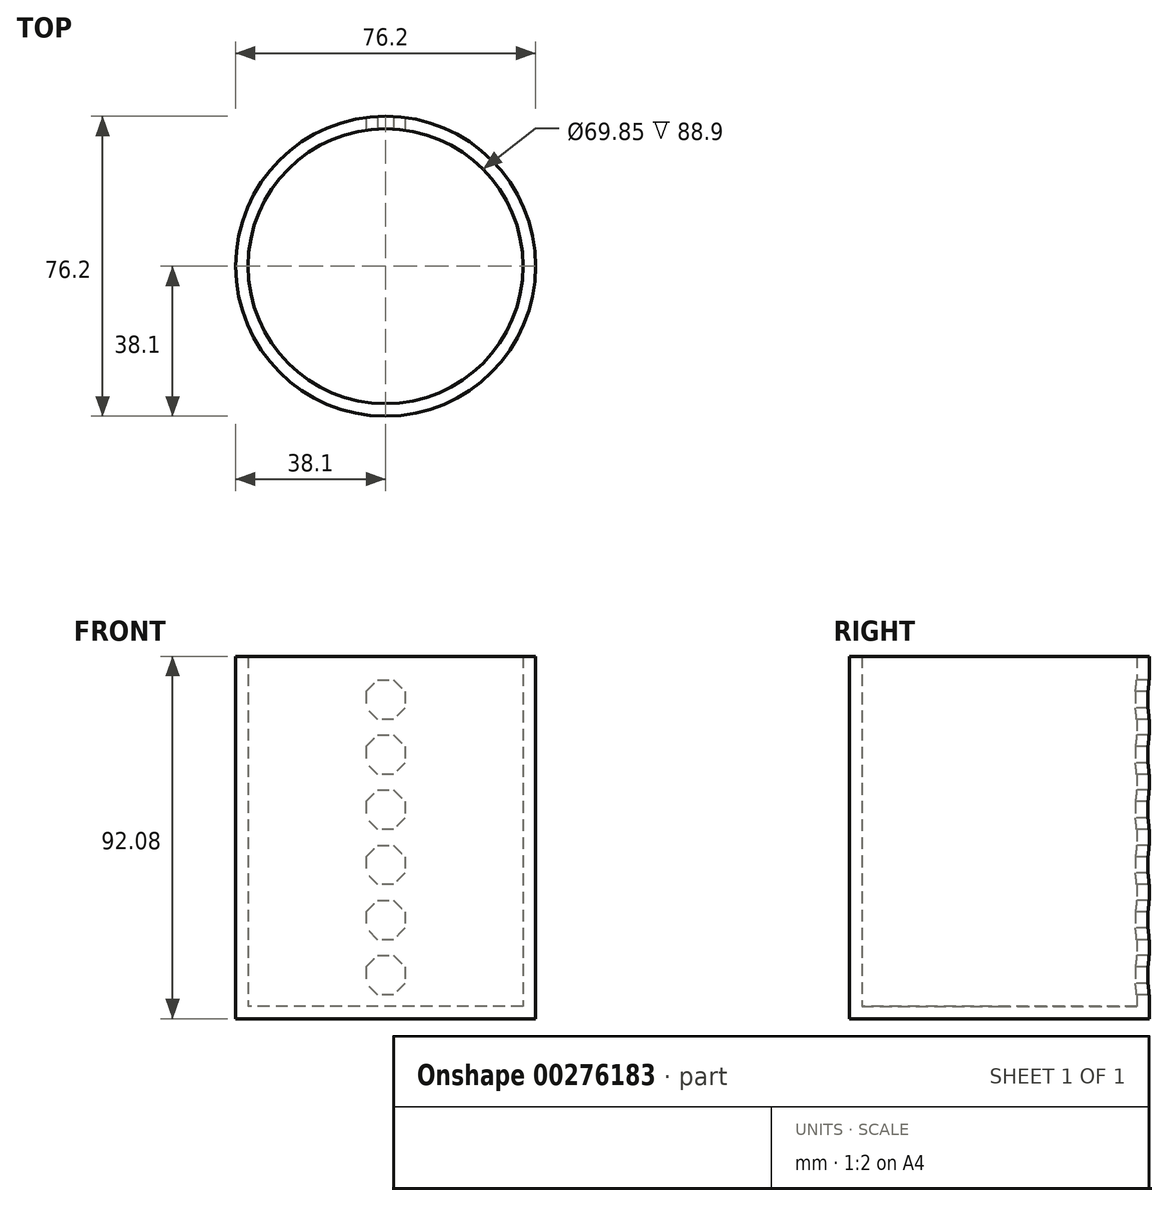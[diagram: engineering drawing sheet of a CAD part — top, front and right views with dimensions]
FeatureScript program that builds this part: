
annotation { "Feature Type Name" : "Feature", "Feature Type Description" : "" }
export const myFeature = defineFeature(function(context is Context, id is Id, definition is map)
    precondition{}
    {
        {
            var Q0;
            Q0=qCreatedBy(makeId("Top.planeOp"),FACE);
            var sketch = newSketch(context, id + "F0", { "sketchPlane" : qUnion([Q0])});
            skCircle(sketch, "E0", {"center": v(0, 0) * mm, "radius": 38.1 * mm});
            skSolve(sketch);
        }
        {
            var Q0;
            Q0=qSketchRegion(id+"F0",true);
            extrude(context, id + "F1", {"entities" : qUnion([Q0]), "depth" : 3.17 * mm});
        }
        {
            var Q0;
            Q0=makeQuery(id+"F1.opExtrude","CAP_FACE",FACE,{"disambiguationData":[OSD([sQuery(id+"F0.wireOp",EDGE,"E0")])],"isStart":false});
            var sketch = newSketch(context, id + "F2", { "sketchPlane" : qUnion([Q0])});
            skCircle(sketch, "E1.0", {"center": v(0, 0) * mm, "radius": 38.1 * mm});
            skCircle(sketch, "E2.0", {"center": v(0, 0) * mm, "radius": 34.93 * mm});
            skSolve(sketch);
        }
        {
            var Q0;
            Q0=qSketchRegion(id+"F2",true);
            extrude(context, id + "F3", {"entities" : qUnion([Q0]), "operationType" : NewBodyOperationType.ADD, "depth" : 88.9 * mm});
        }
        {
            var Q0;
            Q0=qCreatedBy(makeId("Right.planeOp"),FACE);
            var sketch = newSketch(context, id + "F4", { "sketchPlane" : qUnion([Q0])});
            skLineSegment(sketch, "E3", {"start": v(0, 0) * mm, "end": v(0, 120.33) * mm});
            skSolve(sketch);
        }
        {
            var Q0;
            Q0=qCreatedBy(makeId("Front.planeOp"),FACE);
            var sketch = newSketch(context, id + "F5", { "sketchPlane" : qUnion([Q0])});
            skCircle(sketch, "E4.cCircle", {"center": v(0, 81.08) * mm, "radius": 5 * mm, "construction": true});
            skLineSegment(sketch, "E4.0", {"start": v(2.07, 86.07) * mm, "end": v(5, 83.15) * mm});
            skLineSegment(sketch, "E4.1", {"start": v(5, 83.15) * mm, "end": v(5, 79) * mm});
            skLineSegment(sketch, "E4.2", {"start": v(5, 79) * mm, "end": v(2.07, 76.08) * mm});
            skLineSegment(sketch, "E4.3", {"start": v(2.07, 76.08) * mm, "end": v(-2.07, 76.08) * mm});
            skLineSegment(sketch, "E4.4", {"start": v(-2.07, 76.08) * mm, "end": v(-5, 79) * mm});
            skLineSegment(sketch, "E4.5", {"start": v(-5, 79) * mm, "end": v(-5, 83.15) * mm});
            skLineSegment(sketch, "E4.6", {"start": v(-5, 83.15) * mm, "end": v(-2.07, 86.08) * mm});
            skLineSegment(sketch, "E4.7", {"start": v(-2.07, 86.08) * mm, "end": v(2.07, 86.08) * mm});
            skPoint(sketch, "E4.0.midPoint", {"position": v(3.54, 84.61) * mm});
            skLineSegment(sketch, "E5.0.1.0", {"start": v(-2.07, 72.08) * mm, "end": v(2.07, 72.08) * mm});
            skLineSegment(sketch, "E5.0.1.1", {"start": v(2.07, 72.07) * mm, "end": v(5, 69.15) * mm});
            skLineSegment(sketch, "E5.0.1.2", {"start": v(5, 69.15) * mm, "end": v(5, 65) * mm});
            skLineSegment(sketch, "E5.0.1.3", {"start": v(5, 65) * mm, "end": v(2.07, 62.08) * mm});
            skLineSegment(sketch, "E5.0.1.4", {"start": v(2.07, 62.08) * mm, "end": v(-2.07, 62.08) * mm});
            skLineSegment(sketch, "E5.0.1.5", {"start": v(-2.07, 62.08) * mm, "end": v(-5, 65) * mm});
            skLineSegment(sketch, "E5.0.1.6", {"start": v(-5, 65) * mm, "end": v(-5, 69.15) * mm});
            skLineSegment(sketch, "E5.0.1.7", {"start": v(-5, 69.15) * mm, "end": v(-2.07, 72.08) * mm});
            skLineSegment(sketch, "E5.0.2.0", {"start": v(-2.07, 58.08) * mm, "end": v(2.07, 58.08) * mm});
            skLineSegment(sketch, "E5.0.2.1", {"start": v(2.07, 58.07) * mm, "end": v(5, 55.15) * mm});
            skLineSegment(sketch, "E5.0.2.2", {"start": v(5, 55.15) * mm, "end": v(5, 51) * mm});
            skLineSegment(sketch, "E5.0.2.3", {"start": v(5, 51) * mm, "end": v(2.07, 48.08) * mm});
            skLineSegment(sketch, "E5.0.2.4", {"start": v(2.07, 48.08) * mm, "end": v(-2.07, 48.08) * mm});
            skLineSegment(sketch, "E5.0.2.5", {"start": v(-2.07, 48.08) * mm, "end": v(-5, 51) * mm});
            skLineSegment(sketch, "E5.0.2.6", {"start": v(-5, 51) * mm, "end": v(-5, 55.15) * mm});
            skLineSegment(sketch, "E5.0.2.7", {"start": v(-5, 55.15) * mm, "end": v(-2.07, 58.08) * mm});
            skLineSegment(sketch, "E5.0.3.0", {"start": v(-2.07, 44.08) * mm, "end": v(2.07, 44.08) * mm});
            skLineSegment(sketch, "E5.0.3.1", {"start": v(2.07, 44.07) * mm, "end": v(5, 41.15) * mm});
            skLineSegment(sketch, "E5.0.3.2", {"start": v(5, 41.15) * mm, "end": v(5, 37) * mm});
            skLineSegment(sketch, "E5.0.3.3", {"start": v(5, 37) * mm, "end": v(2.07, 34.08) * mm});
            skLineSegment(sketch, "E5.0.3.4", {"start": v(2.07, 34.08) * mm, "end": v(-2.07, 34.08) * mm});
            skLineSegment(sketch, "E5.0.3.5", {"start": v(-2.07, 34.08) * mm, "end": v(-5, 37) * mm});
            skLineSegment(sketch, "E5.0.3.6", {"start": v(-5, 37) * mm, "end": v(-5, 41.15) * mm});
            skLineSegment(sketch, "E5.0.3.7", {"start": v(-5, 41.15) * mm, "end": v(-2.07, 44.08) * mm});
            skLineSegment(sketch, "E5.0.4.0", {"start": v(-2.07, 30.08) * mm, "end": v(2.07, 30.08) * mm});
            skLineSegment(sketch, "E5.0.4.1", {"start": v(2.07, 30.07) * mm, "end": v(5, 27.15) * mm});
            skLineSegment(sketch, "E5.0.4.2", {"start": v(5, 27.15) * mm, "end": v(5, 23) * mm});
            skLineSegment(sketch, "E5.0.4.3", {"start": v(5, 23) * mm, "end": v(2.07, 20.08) * mm});
            skLineSegment(sketch, "E5.0.4.4", {"start": v(2.07, 20.08) * mm, "end": v(-2.07, 20.08) * mm});
            skLineSegment(sketch, "E5.0.4.5", {"start": v(-2.07, 20.08) * mm, "end": v(-5, 23) * mm});
            skLineSegment(sketch, "E5.0.4.6", {"start": v(-5, 23) * mm, "end": v(-5, 27.15) * mm});
            skLineSegment(sketch, "E5.0.4.7", {"start": v(-5, 27.15) * mm, "end": v(-2.07, 30.08) * mm});
            skLineSegment(sketch, "E5.0.5.0", {"start": v(-2.07, 16.08) * mm, "end": v(2.07, 16.08) * mm});
            skLineSegment(sketch, "E5.0.5.1", {"start": v(2.07, 16.07) * mm, "end": v(5, 13.15) * mm});
            skLineSegment(sketch, "E5.0.5.2", {"start": v(5, 13.15) * mm, "end": v(5, 9) * mm});
            skLineSegment(sketch, "E5.0.5.3", {"start": v(5, 9) * mm, "end": v(2.07, 6.08) * mm});
            skLineSegment(sketch, "E5.0.5.4", {"start": v(2.07, 6.08) * mm, "end": v(-2.07, 6.08) * mm});
            skLineSegment(sketch, "E5.0.5.5", {"start": v(-2.07, 6.08) * mm, "end": v(-5, 9) * mm});
            skLineSegment(sketch, "E5.0.5.6", {"start": v(-5, 9) * mm, "end": v(-5, 13.15) * mm});
            skLineSegment(sketch, "E5.0.5.7", {"start": v(-5, 13.15) * mm, "end": v(-2.07, 16.08) * mm});
            skLineSegment(sketch, "E5.direction1", {"start": v(-2.07, 86.08) * mm, "end": v(22.93, 86.08) * mm, "construction": true});
            skLineSegment(sketch, "E5.direction2", {"start": v(-2.07, 86.08) * mm, "end": v(-2.07, 72.08) * mm, "construction": true});
            skSolve(sketch);
        }
        {
            var Q0;
            Q0=qSketchRegion(id+"F5",true);
            extrude(context, id + "F6", {"entities" : qUnion([Q0]), "operationType" : NewBodyOperationType.REMOVE, "endBound" : BoundingType.THROUGH_ALL, "oppositeDirection" : true, "depth" : 25 * mm});
        }
    });
